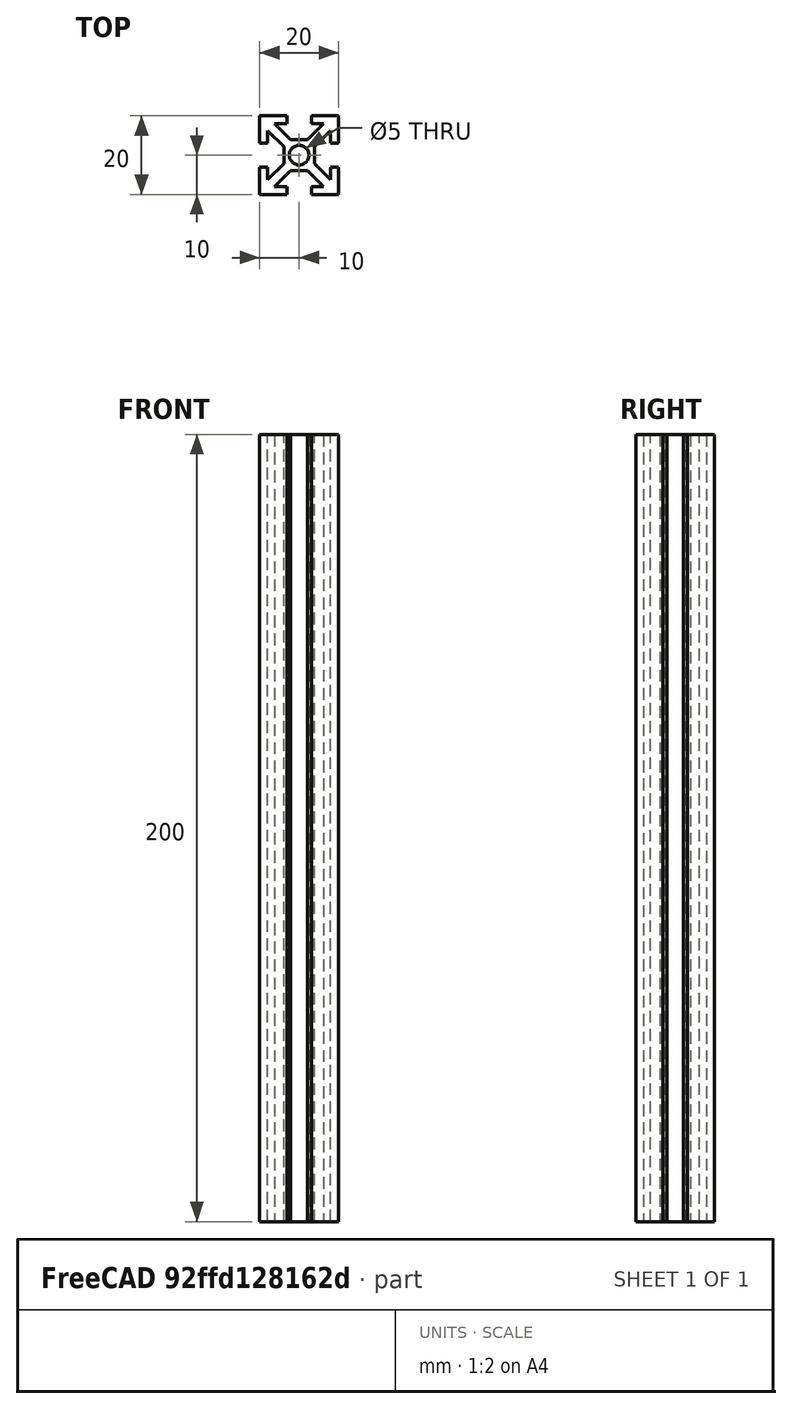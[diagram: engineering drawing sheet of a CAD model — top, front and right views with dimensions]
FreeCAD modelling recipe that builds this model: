
FCSTD DOCUMENT  (FreeCAD 1.0R39109 (Git))
Label: T-Slot_20_width
License: All rights reserved
LicenseURL: http://en.wikipedia.org/wiki/All_rights_reserved
objects: Sketcher::SketchObject×3, PartDesign::Pocket×2, TechDraw::DrawProjGroupItem×2, TechDraw::DrawViewDimension×2, PartDesign::Pad×1, PartDesign::Body×1, TechDraw::DrawSVGTemplate×1, TechDraw::DrawProjGroup×1, TechDraw::DrawPage×1
note: 19 computed .brp shape members not serialized (recipe doc carries the construction recipe); baked Part::Feature solids carry a one-line shape summary decoded from their .brp

FEATURE [Sketcher::SketchObject] Sketch
  ArcFitTolerance = 0
  AttachmentSupport = -> [XY_Plane]
  FullyConstrained = true
  MakeInternals = false
  MapMode = 5
  sketch-geometry (4):
    g0: LineSegment StartX=-10 StartY=10 StartZ=0 EndX=10 EndY=10 EndZ=0
    g1: LineSegment StartX=10 StartY=10 StartZ=0 EndX=10 EndY=-10 EndZ=0
    g2: LineSegment StartX=10 StartY=-10 StartZ=0 EndX=-10 EndY=-10 EndZ=0
    g3: LineSegment StartX=-10 StartY=-10 StartZ=0 EndX=-10 EndY=10 EndZ=0
  constraints (10):
    c: Coincident(g0,g1)
    c: Coincident(g1,g2)
    c: Coincident(g2,g3)
    c: Coincident(g3,g0)
    c: Horizontal(g0)
    c: Vertical(g1)
    c: Symmetric(g2,g1,g-2)
    c: Symmetric(g0,g2,g-1)
    c: Equal(g3,g2)
    c: Distance(g0) = 20
FEATURE [PartDesign::Pad] Pad  label="Change Length Here!"
  AllowMultiFace = false
  Direction = (0,0,1)
  Length = 200
  Length2 = 100
  Profile = -> Sketch
  ReferenceAxis = -> Sketch [N_Axis]
  Refine = true
  Suppressed = false
  Type = 0
FEATURE [Sketcher::SketchObject] Sketch001
  ArcFitTolerance = 0
  AttachmentSupport = -> [Pad]
  ExternalGeometry = -> [Pad]
  FullyConstrained = false
  MakeInternals = false
  MapMode = 5
  Placement = pos=(0,0,200) rot=(0,0,1;0rad)
  sketch-geometry (23):
    g0: LineSegment StartX=-3.1 StartY=10 StartZ=0 EndX=3.1 EndY=10 EndZ=0
    g1: LineSegment StartX=3.1 StartY=10 StartZ=0 EndX=3.1 EndY=8 EndZ=0
    g2: LineSegment [constr] StartX=3.1 StartY=8 StartZ=0 EndX=-3.1 EndY=8 EndZ=0
    g3: LineSegment StartX=-3.1 StartY=8 StartZ=0 EndX=-3.1 EndY=10 EndZ=0
    g4: LineSegment StartX=-3.1 StartY=8 StartZ=0 EndX=-6.23223 EndY=8 EndZ=0
    g5: LineSegment StartX=-6.23223 StartY=8 StartZ=0 EndX=-2.13223 EndY=3.9 EndZ=0
    g6: LineSegment StartX=-2.13223 StartY=3.9 StartZ=0 EndX=2.13223 EndY=3.9 EndZ=0
    g7: LineSegment StartX=2.13223 StartY=3.9 StartZ=0 EndX=6.23223 EndY=8 EndZ=0
    g8: LineSegment StartX=6.23223 StartY=8 StartZ=0 EndX=3.1 EndY=8 EndZ=0
    g9: LineSegment [constr] StartX=-3.9 StartY=3.9 StartZ=0 EndX=3.9 EndY=3.9 EndZ=0
    g10: LineSegment [constr] StartX=3.9 StartY=3.9 StartZ=0 EndX=3.9 EndY=-3.9 EndZ=0
    g11: LineSegment [constr] StartX=3.9 StartY=-3.9 StartZ=0 EndX=-3.9 EndY=-3.9 EndZ=0
    g12: LineSegment [constr] StartX=-3.9 StartY=-3.9 StartZ=0 EndX=-3.9 EndY=3.9 EndZ=0
    g13: Circle CenterX=0 CenterY=0 CenterZ=0 NormalX=0 NormalY=0 NormalZ=1 AngleXU=0 Radius=2.5
    g14: LineSegment [constr] StartX=3.9 StartY=3.9 StartZ=0 EndX=3.01612 EndY=4.78388 EndZ=0
    g15: LineSegment StartX=-3.1 StartY=-8 StartZ=0 EndX=-6.23223 EndY=-8 EndZ=0
    g16: LineSegment StartX=6.23223 StartY=-8 StartZ=0 EndX=3.1 EndY=-8 EndZ=0
    g17: LineSegment StartX=3.1 StartY=-10 StartZ=0 EndX=3.1 EndY=-8 EndZ=0
    g18: LineSegment StartX=-3.1 StartY=-10 StartZ=0 EndX=3.1 EndY=-10 EndZ=0
    g19: LineSegment StartX=-3.1 StartY=-8 StartZ=0 EndX=-3.1 EndY=-10 EndZ=0
    g20: LineSegment StartX=-6.23223 StartY=-8 StartZ=0 EndX=-2.13223 EndY=-3.9 EndZ=0
    g21: LineSegment StartX=-2.13223 StartY=-3.9 StartZ=0 EndX=2.13223 EndY=-3.9 EndZ=0
    g22: LineSegment StartX=2.13223 StartY=-3.9 StartZ=0 EndX=6.23223 EndY=-8 EndZ=0
  constraints (55):
    c: Coincident(g0,g1)
    c: Coincident(g1,g2)
    c: Coincident(g2,g3)
    c: Coincident(g3,g0)
    c: Horizontal(g2)
    c: Vertical(g1)
    c: Vertical(g3)
    c: PointOnObject(g0,g-3)
    c: Symmetric(g0,g0,g-2)
    c: Distance(g0) = 6.2
    c: Distance(g3) = 2
    c: Coincident(g3,g4)
    c: Horizontal(g4)
    c: Coincident(g4,g5)
    c: Coincident(g5,g6)
    c: Coincident(g6,g7)
    c: Coincident(g7,g8)
    c: Coincident(g8,g1)
    c: Horizontal(g8)
    c: Symmetric(g5,g6,g-2)
    c: Equal(g4,g8)
    c: Coincident(g9,g10)
    c: Coincident(g10,g11)
    c: Coincident(g11,g12)
    c: Coincident(g12,g9)
    c: Horizontal(g9)
    c: Vertical(g12)
    c: Equal(g9,g12)
    c: Symmetric(g11,g10,g-2)
    c: Symmetric(g9,g10,g-1)
    c: Distance(g9) = 7.8
    c: Coincident(g13,g-1)
    c: Radius(g13) = 2.5
    c: DistanceY(g6,g0) = 6.1
    c: Coincident(g14,g9)
    c: PointOnObject(g14,g7)
    c: Perpendicular(g7,g14)
    c: Distance(g14) = 1.25
    c: Angle(g6,g5) = 2.35619
    c: Coincident(g18,g17)
    c: Coincident(g19,g18)
    c: Vertical(g17)
    c: Vertical(g19)
    c: Distance(g18) = 6.2
    c: Distance(g19) = 2
    c: Coincident(g19,g15)
    c: Horizontal(g15)
    c: Coincident(g15,g20)
    c: Coincident(g20,g21)
    c: Coincident(g21,g22)
    c: Coincident(g22,g16)
    c: Coincident(g16,g17)
    c: Horizontal(g16)
    c: Equal(g15,g16)
    c: Angle(g21,g20) = -2.35619
FEATURE [PartDesign::Pocket] Pocket  label="Top & Bottom Slots"
  AllowMultiFace = false
  BaseFeature = -> Pad
  Direction = (0,0,-1)
  Length = 5
  Length2 = 100
  Profile = -> Sketch001
  Refine = true
  Suppressed = false
  Type = 1
FEATURE [Sketcher::SketchObject] Sketch002
  ArcFitTolerance = 0
  AttachmentSupport = -> [Pocket]
  ExternalGeometry = -> [Pocket]
  FullyConstrained = false
  MakeInternals = false
  MapMode = 5
  Placement = pos=(0,0,0) rot=(1,0,0;3.14159rad)
  sketch-geometry (19):
    g0: LineSegment StartX=-10 StartY=-3.1 StartZ=0 EndX=-8 EndY=-3.1 EndZ=0
    g1: LineSegment [constr] StartX=-8 StartY=-3.1 StartZ=0 EndX=-8 EndY=3.1 EndZ=0
    g2: LineSegment StartX=-8 StartY=3.1 StartZ=0 EndX=-10 EndY=3.1 EndZ=0
    g3: LineSegment StartX=-10 StartY=3.1 StartZ=0 EndX=-10 EndY=-3.1 EndZ=0
    g4: LineSegment StartX=-8 StartY=-3.1 StartZ=0 EndX=-8 EndY=-6.23223 EndZ=0
    g5: LineSegment StartX=-8 StartY=-6.23223 StartZ=0 EndX=-3.9 EndY=-2.13223 EndZ=0
    g6: LineSegment StartX=-3.9 StartY=-2.13223 StartZ=0 EndX=-3.9 EndY=2.13223 EndZ=0
    g7: LineSegment StartX=-3.9 StartY=2.13223 StartZ=0 EndX=-8 EndY=6.23223 EndZ=0
    g8: LineSegment StartX=-8 StartY=6.23223 StartZ=0 EndX=-8 EndY=3.1 EndZ=0
    g9: LineSegment [constr] StartX=-2.13223 StartY=3.9 StartZ=0 EndX=-3.9 EndY=2.13223 EndZ=0
    g10: LineSegment [constr] StartX=2.13223 StartY=3.9 StartZ=0 EndX=3.9 EndY=2.13223 EndZ=0
    g11: LineSegment StartX=3.9 StartY=-2.13223 StartZ=0 EndX=3.9 EndY=2.13223 EndZ=0
    g12: LineSegment StartX=8 StartY=-6.23223 StartZ=0 EndX=3.9 EndY=-2.13223 EndZ=0
    g13: LineSegment StartX=3.9 StartY=2.13223 StartZ=0 EndX=8 EndY=6.23223 EndZ=0
    g14: LineSegment StartX=8 StartY=6.23223 StartZ=0 EndX=8 EndY=3.1 EndZ=0
    g15: LineSegment StartX=8 StartY=3.1 StartZ=0 EndX=10 EndY=3.1 EndZ=0
    g16: LineSegment StartX=10 StartY=3.1 StartZ=0 EndX=10 EndY=-3.1 EndZ=0
    g17: LineSegment StartX=10 StartY=-3.1 StartZ=0 EndX=8 EndY=-3.1 EndZ=0
    g18: LineSegment StartX=8 StartY=-3.1 StartZ=0 EndX=8 EndY=-6.23223 EndZ=0
  constraints (43):
    c: Coincident(g0,g1)
    c: Coincident(g1,g2)
    c: Coincident(g2,g3)
    c: Coincident(g3,g0)
    c: Horizontal(g0)
    c: Horizontal(g2)
    c: Vertical(g1)
    c: PointOnObject(g0,g-3)
    c: Symmetric(g2,g0,g-1)
    c: Distance(g3) = 6.2
    c: Distance(g0) = 2
    c: Coincident(g0,g4)
    c: Vertical(g4)
    c: Coincident(g4,g5)
    c: Coincident(g5,g6)
    c: Coincident(g6,g7)
    c: Coincident(g7,g8)
    c: Coincident(g8,g2)
    c: Vertical(g8)
    c: Equal(g4,g8)
    c: Symmetric(g6,g5,g-1)
    c: DistanceX(g2,g6) = 6.1
    c: Angle(g6,g5) = 2.35619
    c: Coincident(g9,g-4)
    c: Perpendicular(g-4,g9)
    c: Coincident(g6,g9)
    c: Coincident(g15,g16)
    c: Coincident(g16,g17)
    c: Horizontal(g17)
    c: Horizontal(g15)
    c: Distance(g16) = 6.2
    c: Distance(g17) = 2
    c: Coincident(g17,g18)
    c: Vertical(g18)
    c: Coincident(g18,g12)
    c: Coincident(g12,g11)
    c: Coincident(g11,g13)
    c: Coincident(g13,g14)
    c: Coincident(g14,g15)
    c: Vertical(g14)
    c: Equal(g18,g14)
    c: Angle(g11,g12) = -2.35619
    c: Coincident(g11,g10)
FEATURE [PartDesign::Pocket] Pocket001  label="R&L Slots"
  AllowMultiFace = false
  BaseFeature = -> Pocket
  Direction = (0,0,1)
  Length = 5
  Length2 = 100
  Profile = -> Sketch002
  Refine = true
  Suppressed = false
  Type = 1
FEATURE [PartDesign::Body] Body  label="Tslot20_wid"
  AllowCompound = false
  Group = -> [Sketch,Pad,Sketch001,Pocket,Sketch002,Pocket001]
  Origin = -> Origin
  Tip = -> Pocket001
FEATURE [TechDraw::DrawSVGTemplate] Template
  EditableTexts = approval_person=B. Hecate; creator=Djordje Vujic; date_of_issue=1/21/2025; document_type=Assembly Drawing; general_tolerances=ISO 2768-m; identification_number=DN; language_code=EN; part_material=Stainless steel Mat.No. 1.4301; revision_index=AAA; sheet_number=1 / 6; sheet_scale=1 : 2; title=T-Slot_20_width
  Height = 297
  Orientation = 0
  Template = D:/Program Files/FreeCAD 1.0/data/Mod/TechDraw/Templates/A4_Portrait_ISO5457_minimal.svg
  Width = 210
FEATURE [TechDraw::DrawProjGroupItem] ProjItem  label="Front"
  CoarseView = false
  Direction = (0,-1,0)
  Focus = 100
  HardHidden = false
  IsoCount = 0
  IsoHidden = false
  IsoVisible = false
  LockPosition = true
  Perspective = false
  Rotation = 0
  RotationVector = (1,0,0)
  Scale = 0.5
  ScaleType = 0
  ScrubCount = 1
  SeamHidden = false
  SeamVisible = false
  SmoothHidden = false
  SmoothVisible = true
  Source = -> [Body]
  Type = 0
  X = 0
  XDirection = (1,0,0)
  Y = 0
FEATURE [TechDraw::DrawProjGroupItem] ProjItem001  label="Bottom"
  CoarseView = false
  Direction = (0,0,-1)
  Focus = 100
  HardHidden = false
  IsoCount = 0
  IsoHidden = false
  IsoVisible = false
  LockPosition = false
  Perspective = false
  Rotation = 0
  RotationVector = (1,0,0)
  Scale = 0.5
  ScaleType = 0
  ScrubCount = 1
  SeamHidden = false
  SeamVisible = false
  SmoothHidden = false
  SmoothVisible = true
  Source = -> [Body]
  Type = 5
  X = 0
  XDirection = (1,0,0)
  Y = 70
FEATURE [TechDraw::DrawProjGroup] ProjGroup
  Anchor = -> ProjItem
  AutoDistribute = true
  LockPosition = false
  ProjectionType = 0
  Rotation = 0
  Scale = 0.5
  ScaleType = 2
  Source = -> [Body]
  Views = -> [ProjItem,ProjItem001]
  X = 106.426
  Y = 132.809
  spacingX = 15
  spacingY = 15
FEATURE [TechDraw::DrawViewDimension] Dimension
  AngleOverride = false
  Arbitrary = false
  ArbitraryTolerances = false
  BoxCorners = (2) [(-5,-50,0),(5,50,0)]
  EqualTolerance = true
  ExtensionAngle = 0
  FormatSpec = %.2w
  FormatSpecOverTolerance = %+.2w
  FormatSpecUnderTolerance = %+.2w
  Inverted = false
  LineAngle = 0
  LockPosition = false
  MeasureType = 1
  OverTolerance = 0
  References2D = -> [ProjItem]
  Rotation = 0
  ScaleType = 0
  TheoreticalExact = false
  Type = 2
  UnderTolerance = 0
  X = 38.4564
  Y = 0
FEATURE [TechDraw::DrawViewDimension] Dimension001
  AngleOverride = false
  Arbitrary = false
  ArbitraryTolerances = false
  BoxCorners = (2) [(-5,-5,0),(5,5,0)]
  EqualTolerance = true
  ExtensionAngle = 0
  FormatSpec = %.2w
  FormatSpecOverTolerance = %+.2w
  FormatSpecUnderTolerance = %+.2w
  Inverted = false
  LineAngle = 0
  LockPosition = false
  MeasureType = 1
  OverTolerance = 0
  References2D = -> [ProjItem001]
  Rotation = 0
  ScaleType = 0
  TheoreticalExact = false
  Type = 2
  UnderTolerance = 0
  X = 34.5605
  Y = 0
FEATURE [TechDraw::DrawPage] Page
  KeepUpdated = true
  NextBalloonIndex = 1
  ProjectionType = 0
  Template = -> Template
  Views = -> [ProjGroup,Dimension,Dimension001]
